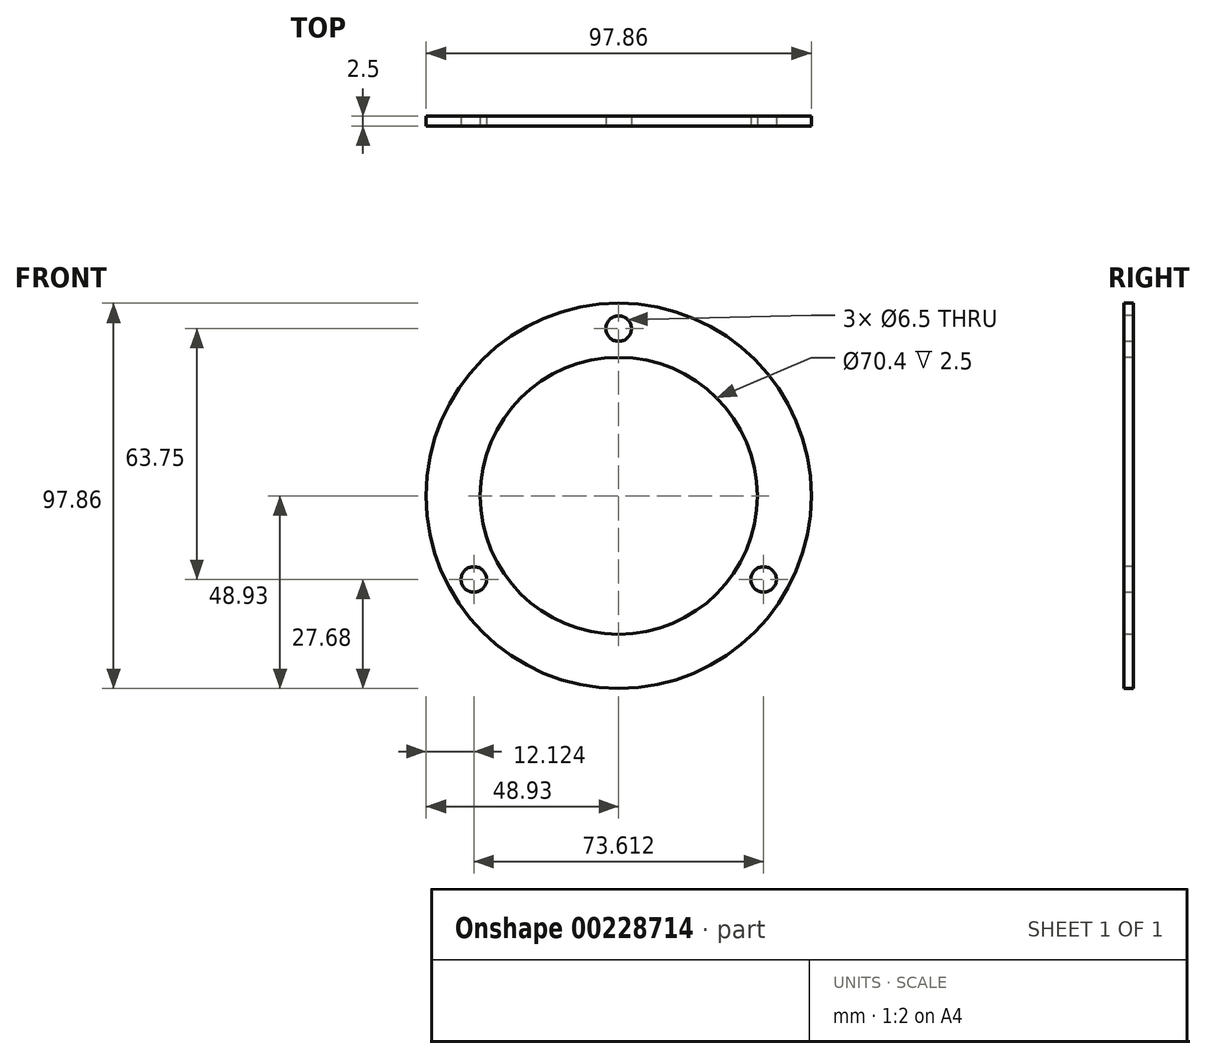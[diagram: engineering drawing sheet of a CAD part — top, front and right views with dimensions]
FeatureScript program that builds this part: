
annotation { "Feature Type Name" : "Feature", "Feature Type Description" : "" }
export const myFeature = defineFeature(function(context is Context, id is Id, definition is map)
    precondition{}
    {
        {
            var Q0;
            Q0=qCreatedBy(makeId("Front.planeOp"),FACE);
            var sketch = newSketch(context, id + "F0", { "sketchPlane" : qUnion([Q0])});
            skCircle(sketch, "E0", {"center": v(0, 0) * mm, "radius": 35.2 * mm});
            skCircle(sketch, "E1", {"center": v(0, 0) * mm, "radius": 48.92 * mm});
            skSolve(sketch);
        }
        {
            var Q0;
            Q0=makeQuery(id+"F0.imprint","IMPRINT",FACE,{"disambiguationData":[TD([[makeQuery(id+"F0.imprint","IMPRINT",EDGE,{"derivedFrom":sQuery(id+"F0.wireOp",EDGE,"E0")}),-1.0]])]});
            extrude(context, id + "F1", {"entities" : qUnion([Q0]), "oppositeDirection" : true, "depth" : 2.5 * mm});
        }
        {
            var Q0;
            Q0=makeQuery(id+"F1.opExtrude","CAP_FACE",FACE,{"disambiguationData":[OSD([sQuery(id+"F0.wireOp",EDGE,"E0"),sQuery(id+"F0.wireOp",EDGE,"E1")])],"isStart":true});
            var sketch = newSketch(context, id + "F2", { "sketchPlane" : qUnion([Q0])});
            skPoint(sketch, "E2", {"position": v(0, 42.5) * mm});
            skPoint(sketch, "E3", {"position": v(-36.8, -21.25) * mm});
            skPoint(sketch, "E4", {"position": v(36.8, -21.25) * mm});
            skCircle(sketch, "E5", {"center": v(0, 0) * mm, "radius": 42.5 * mm});
            skLineSegment(sketch, "E6", {"start": v(0, 42.5) * mm, "end": v(0, 0) * mm});
            skLineSegment(sketch, "E7", {"start": v(0, 0) * mm, "end": v(-36.8, -21.25) * mm});
            skLineSegment(sketch, "E8", {"start": v(0, 0) * mm, "end": v(36.8, -21.25) * mm});
            skSolve(sketch);
        }
        {
            var Q0;
            Q0=sQuery(id+"F2.wireOp",VERTEX,"E2");
            var Q1;
            Q1=sQuery(id+"F2.wireOp",VERTEX,"E3");
            var Q2;
            Q2=sQuery(id+"F2.wireOp",VERTEX,"E4");
            var Q3;
            Q3=makeQuery(id+"F1.opExtrude","SWEPT_BODY",BODY,{"disambiguationData":[OSD([sQuery(id+"F0.wireOp",EDGE,"E0"),sQuery(id+"F0.wireOp",EDGE,"E1")])]});
            hole(context, id + "F3", {"style" : HoleStyle.SIMPLE, "endStyle" : HoleEndStyle.THROUGH, "holeDiameter" : 6.5 * mm, "startFromSketch" : true, "locations" : qUnion([Q0, Q1, Q2]), "scope" : qUnion([Q3]), "isTappedThrough" : true});
        }
    });
